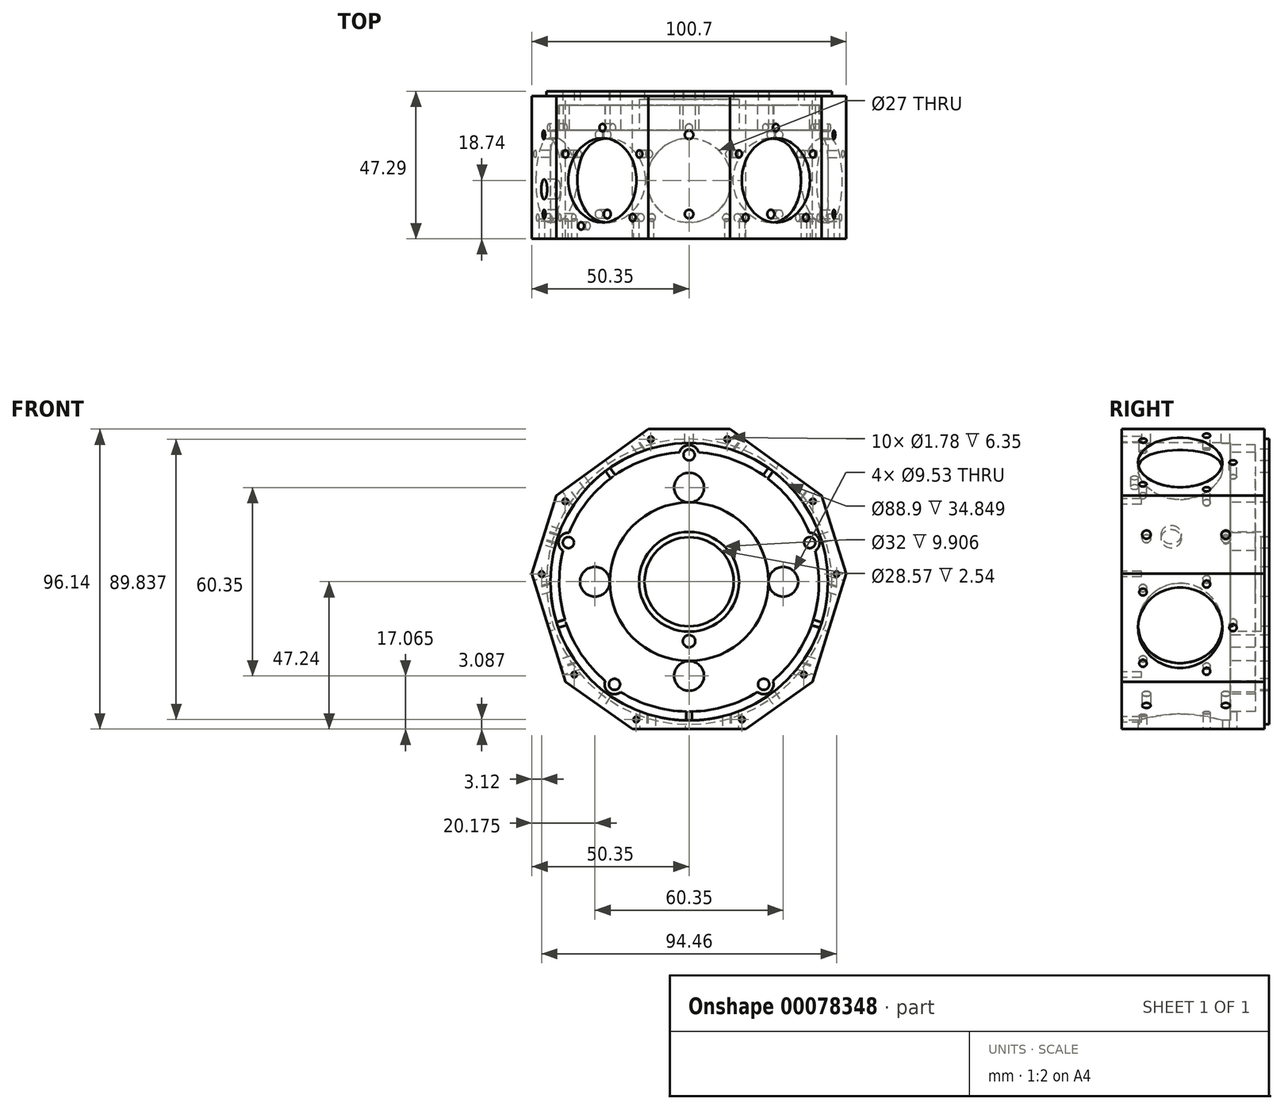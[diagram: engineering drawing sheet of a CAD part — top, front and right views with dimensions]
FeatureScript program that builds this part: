
annotation { "Feature Type Name" : "Feature", "Feature Type Description" : "" }
export const myFeature = defineFeature(function(context is Context, id is Id, definition is map)
    precondition{}
    {
        {
            var Q0;
            Q0=qCreatedBy(makeId("Front.planeOp"),FACE);
            var sketch = newSketch(context, id + "F0", { "sketchPlane" : qUnion([Q0])});
            skLineSegment(sketch, "E0", {"start": v(0, 0) * mm, "end": v(0, 48.9) * mm, "construction": true});
            skCircle(sketch, "E1", {"center": v(0, 0) * mm, "radius": 47.3 * mm, "construction": true});
            skLineSegment(sketch, "E2", {"start": v(0, 0) * mm, "end": v(0, -54.83) * mm, "construction": true});
            skCircle(sketch, "E3", {"center": v(0, 0) * mm, "radius": 44.45 * mm, "construction": true});
            skLineSegment(sketch, "E4", {"start": v(0, 48.9) * mm, "end": v(-13.1, 48.9) * mm});
            skLineSegment(sketch, "E5", {"start": v(-13.1, 48.9) * mm, "end": v(-42.47, 27.58) * mm});
            skLineSegment(sketch, "E6", {"start": v(0, -47.24) * mm, "end": v(-18.14, -47.24) * mm});
            skLineSegment(sketch, "E7", {"start": v(-18.14, -47.24) * mm, "end": v(-39.57, -32.04) * mm});
            skLineSegment(sketch, "E8", {"start": v(-39.57, -32.04) * mm, "end": v(-50.35, 2.64) * mm});
            skLineSegment(sketch, "E9", {"start": v(-50.35, 2.64) * mm, "end": v(-42.47, 27.58) * mm});
            skLineSegment(sketch, "E10.MirrorCS", {"start": v(0, 48.9) * mm, "end": v(13.1, 48.9) * mm});
            skLineSegment(sketch, "E11.MirrorCS", {"start": v(13.1, 48.9) * mm, "end": v(42.47, 27.58) * mm});
            skLineSegment(sketch, "E12.MirrorCS", {"start": v(50.35, 2.64) * mm, "end": v(42.47, 27.58) * mm});
            skLineSegment(sketch, "E13.MirrorCS", {"start": v(39.57, -32.04) * mm, "end": v(50.35, 2.64) * mm});
            skLineSegment(sketch, "E14.MirrorCS", {"start": v(18.14, -47.24) * mm, "end": v(39.57, -32.04) * mm});
            skLineSegment(sketch, "E15.MirrorCS", {"start": v(0, -47.24) * mm, "end": v(18.14, -47.24) * mm});
            skSolve(sketch);
        }
        {
            var Q0;
            Q0 = qSketchRegion(id + "F0", true);
            extrude(context, id + "F1", {"entities" : qUnion([Q0]), "depth" : 47.3 * mm});
        }
        {
            var Q0;
            Q0=makeQuery(id+"F1.opExtrude","CAP_FACE",FACE,{"disambiguationData":[OSD([sQuery(id+"F0.wireOp",EDGE,"E4"),sQuery(id+"F0.wireOp",EDGE,"E5"),sQuery(id+"F0.wireOp",EDGE,"E6"),sQuery(id+"F0.wireOp",EDGE,"E7"),sQuery(id+"F0.wireOp",EDGE,"E8"),sQuery(id+"F0.wireOp",EDGE,"E9"),sQuery(id+"F0.wireOp",EDGE,"E10.MirrorCS"),sQuery(id+"F0.wireOp",EDGE,"E11.MirrorCS"),sQuery(id+"F0.wireOp",EDGE,"E12.MirrorCS"),sQuery(id+"F0.wireOp",EDGE,"E13.MirrorCS"),sQuery(id+"F0.wireOp",EDGE,"E14.MirrorCS"),sQuery(id+"F0.wireOp",EDGE,"E15.MirrorCS")])],"isStart":false});
            var sketch = newSketch(context, id + "F2", { "sketchPlane" : qUnion([Q0])});
            skCircle(sketch, "E16", {"center": v(0, 0) * mm, "radius": 44.45 * mm});
            skSolve(sketch);
        }
        {
            var Q0;
            Q0 = qSketchRegion(id + "F2", true);
            extrude(context, id + "F3", {"entities" : qUnion([Q0]), "operationType" : NewBodyOperationType.REMOVE, "oppositeDirection" : true, "depth" : 34.85 * mm});
        }
        {
            var Q0;
            Q0=makeQuery(id+"F3.boolean.opBoolean","COPY",FACE,{"derivedFrom":makeQuery(id+"F3.opExtrude","CAP_FACE",FACE,{"disambiguationData":[OSD([sQuery(id+"F2.wireOp",EDGE,"E16")])],"isStart":false})});
            var sketch = newSketch(context, id + "F4", { "sketchPlane" : qUnion([Q0])});
            skCircle(sketch, "E17", {"center": v(0, 0) * mm, "radius": 40.64 * mm, "construction": true});
            skArc(sketch, "E18", {"start": v(3.06, 41.48) * mm, "mid": v(0, 43.82) * mm, "end": v(-3.06, 41.48) * mm});
            skArc(sketch, "E19.1.0", {"start": v(-38.5, 15.73) * mm, "mid": v(-41.67, 13.54) * mm, "end": v(-40.4, 9.9) * mm});
            skArc(sketch, "E19.2.0", {"start": v(-26.86, -31.76) * mm, "mid": v(-25.75, -35.45) * mm, "end": v(-21.9, -35.36) * mm});
            skArc(sketch, "E19.3.0", {"start": v(21.9, -35.36) * mm, "mid": v(25.75, -35.45) * mm, "end": v(26.86, -31.76) * mm});
            skArc(sketch, "E19.4.0", {"start": v(40.4, 9.9) * mm, "mid": v(41.67, 13.54) * mm, "end": v(38.5, 15.73) * mm});
            skArc(sketch, "E20", {"start": v(-40.4, 9.9) * mm, "mid": v(-39.56, -12.85) * mm, "end": v(-26.86, -31.76) * mm});
            skArc(sketch, "E21.trimOffspring", {"start": v(-3.06, 41.48) * mm, "mid": v(-24.45, 33.65) * mm, "end": v(-38.5, 15.73) * mm});
            skArc(sketch, "E22.trimOffspring", {"start": v(38.5, 15.73) * mm, "mid": v(24.45, 33.65) * mm, "end": v(3.06, 41.48) * mm});
            skArc(sketch, "E23.trimOffspring", {"start": v(-21.9, -35.36) * mm, "mid": v(0, -41.6) * mm, "end": v(21.9, -35.36) * mm});
            skArc(sketch, "E24.trimOffspring", {"start": v(26.86, -31.76) * mm, "mid": v(39.56, -12.85) * mm, "end": v(40.4, 9.9) * mm});
            skCircle(sketch, "E25", {"center": v(0, 0) * mm, "radius": 25.4 * mm});
            skSolve(sketch);
        }
        {
            var Q0;
            Q0 = qSketchRegion(id + "F4", true);
            extrude(context, id + "F5", {"entities" : qUnion([Q0]), "operationType" : NewBodyOperationType.REMOVE, "oppositeDirection" : true, "depth" : 8 * mm});
        }
        {
            var Q0;
            Q0=makeQuery(id+"F5.boolean.opBoolean","COPY",FACE,{"derivedFrom":makeQuery(id+"F5.opExtrude","CAP_FACE",FACE,{"disambiguationData":[OSD([sQuery(id+"F4.wireOp",EDGE,"E18"),sQuery(id+"F4.wireOp",EDGE,"E19.1.0"),sQuery(id+"F4.wireOp",EDGE,"E19.2.0"),sQuery(id+"F4.wireOp",EDGE,"E19.3.0"),sQuery(id+"F4.wireOp",EDGE,"E19.4.0"),sQuery(id+"F4.wireOp",EDGE,"E20"),sQuery(id+"F4.wireOp",EDGE,"E21.trimOffspring"),sQuery(id+"F4.wireOp",EDGE,"E22.trimOffspring"),sQuery(id+"F4.wireOp",EDGE,"E23.trimOffspring"),sQuery(id+"F4.wireOp",EDGE,"E24.trimOffspring")])],"isStart":false})});
            var sketch = newSketch(context, id + "F6", { "sketchPlane" : qUnion([Q0])});
            skCircle(sketch, "E26", {"center": v(0, 0) * mm, "radius": 40.64 * mm, "construction": true});
            skCircle(sketch, "E27", {"center": v(0, 40.64) * mm, "radius": 1.8 * mm});
            skCircle(sketch, "E28.1.0", {"center": v(-38.65, 12.56) * mm, "radius": 1.8 * mm});
            skCircle(sketch, "E28.2.0", {"center": v(-23.89, -32.88) * mm, "radius": 1.8 * mm});
            skCircle(sketch, "E28.3.0", {"center": v(23.89, -32.88) * mm, "radius": 1.8 * mm});
            skCircle(sketch, "E28.4.0", {"center": v(38.65, 12.56) * mm, "radius": 1.8 * mm});
            skSolve(sketch);
        }
        {
            var Q0;
            Q0 = qSketchRegion(id + "F6", true);
            extrude(context, id + "F7", {"entities" : qUnion([Q0]), "operationType" : NewBodyOperationType.REMOVE, "oppositeDirection" : true, "depth" : 25.4 * mm});
        }
        {
            var Q0;
            Q0=makeQuery(id+"F5.boolean.opBoolean","SPLIT",FACE,{"disambiguationData":[TD([makeQuery(id+"F5.opExtrude","SWEPT_FACE",FACE,{"disambiguationData":[OSD([sQuery(id+"F4.wireOp",EDGE,"E25")])]})])],"derivedFrom":makeQuery(id+"F3.boolean.opBoolean","COPY",FACE,{"derivedFrom":makeQuery(id+"F3.opExtrude","CAP_FACE",FACE,{"disambiguationData":[OSD([sQuery(id+"F2.wireOp",EDGE,"E16")])],"isStart":false})})});
            var sketch = newSketch(context, id + "F8", { "sketchPlane" : qUnion([Q0])});
            skCircle(sketch, "E29", {"center": v(0, 0) * mm, "radius": 16 * mm});
            skSolve(sketch);
        }
        {
            var Q0;
            Q0 = qSketchRegion(id + "F8", true);
            extrude(context, id + "F9", {"entities" : qUnion([Q0]), "operationType" : NewBodyOperationType.REMOVE, "oppositeDirection" : true, "depth" : 9.9 * mm});
        }
        {
            var Q0;
            Q0=makeQuery(id+"F9.boolean.opBoolean","COPY",FACE,{"derivedFrom":makeQuery(id+"F9.opExtrude","CAP_FACE",FACE,{"disambiguationData":[OSD([sQuery(id+"F8.wireOp",EDGE,"E29")])],"isStart":false})});
            var sketch = newSketch(context, id + "F10", { "sketchPlane" : qUnion([Q0])});
            skCircle(sketch, "E30", {"center": v(0, 0) * mm, "radius": 14.29 * mm});
            skSolve(sketch);
        }
        {
            var Q0;
            Q0 = qSketchRegion(id + "F10", true);
            extrude(context, id + "F11", {"entities" : qUnion([Q0]), "operationType" : NewBodyOperationType.REMOVE, "oppositeDirection" : true, "depth" : 25.4 * mm});
        }
        {
            var Q0;
            Q0=makeQuery(id+"F5.boolean.opBoolean","SPLIT",FACE,{"disambiguationData":[TD([makeQuery(id+"F5.opExtrude","SWEPT_FACE",FACE,{"disambiguationData":[OSD([sQuery(id+"F4.wireOp",EDGE,"E25")])]})])],"derivedFrom":makeQuery(id+"F3.boolean.opBoolean","COPY",FACE,{"derivedFrom":makeQuery(id+"F3.opExtrude","CAP_FACE",FACE,{"disambiguationData":[OSD([sQuery(id+"F2.wireOp",EDGE,"E16")])],"isStart":false})})});
            var sketch = newSketch(context, id + "F12", { "sketchPlane" : qUnion([Q0])});
            skLineSegment(sketch, "E31", {"start": v(0, 0) * mm, "end": v(0, -19.05) * mm});
            skCircle(sketch, "E32", {"center": v(0, -19.05) * mm, "radius": 1.98 * mm});
            skSolve(sketch);
        }
        {
            var Q0;
            Q0 = qSketchRegion(id + "F12", true);
            extrude(context, id + "F13", {"entities" : qUnion([Q0]), "operationType" : NewBodyOperationType.REMOVE, "oppositeDirection" : true, "depth" : 25.4 * mm});
        }
        {
            var Q0;
            Q0=makeQuery(id+"F5.boolean.opBoolean","COPY",FACE,{"derivedFrom":makeQuery(id+"F5.opExtrude","CAP_FACE",FACE,{"disambiguationData":[OSD([sQuery(id+"F4.wireOp",EDGE,"E18"),sQuery(id+"F4.wireOp",EDGE,"E19.1.0"),sQuery(id+"F4.wireOp",EDGE,"E19.2.0"),sQuery(id+"F4.wireOp",EDGE,"E19.3.0"),sQuery(id+"F4.wireOp",EDGE,"E19.4.0"),sQuery(id+"F4.wireOp",EDGE,"E20"),sQuery(id+"F4.wireOp",EDGE,"E21.trimOffspring"),sQuery(id+"F4.wireOp",EDGE,"E22.trimOffspring"),sQuery(id+"F4.wireOp",EDGE,"E23.trimOffspring"),sQuery(id+"F4.wireOp",EDGE,"E24.trimOffspring"),sQuery(id+"F4.wireOp",EDGE,"E25")])],"isStart":false})});
            var sketch = newSketch(context, id + "F14", { "sketchPlane" : qUnion([Q0])});
            skCircle(sketch, "E33", {"center": v(0, 0) * mm, "radius": 30.18 * mm, "construction": true});
            skCircle(sketch, "E34", {"center": v(0, 30.18) * mm, "radius": 4.76 * mm});
            skCircle(sketch, "E35.1.0", {"center": v(-30.18, 0) * mm, "radius": 4.76 * mm});
            skCircle(sketch, "E35.2.0", {"center": v(0, -30.18) * mm, "radius": 4.76 * mm});
            skCircle(sketch, "E35.3.0", {"center": v(30.18, 0) * mm, "radius": 4.76 * mm});
            skSolve(sketch);
        }
        {
            var Q0;
            Q0 = qSketchRegion(id + "F14", true);
            var Q1;
            Q1=sQuery(id+"F14.wireOp",EDGE,"E34");
            extrude(context, id + "F15", {"entities" : qUnion([Q0]), "operationType" : NewBodyOperationType.REMOVE, "surfaceEntities" : qUnion([Q1]), "oppositeDirection" : true, "depth" : 25.4 * mm});
        }
        {
            var Q0;
            Q0=makeQuery(id+"F1.opExtrude","SWEPT_FACE",FACE,{"disambiguationData":[OSD([sQuery(id+"F0.wireOp",EDGE,"E6"),sQuery(id+"F0.wireOp",EDGE,"E15.MirrorCS")])]});
            var sketch = newSketch(context, id + "F16", { "sketchPlane" : qUnion([Q0])});
            skLineSegment(sketch, "E36", {"start": v(0, 0) * mm, "end": v(0, 28.55) * mm, "construction": true});
            skCircle(sketch, "E37", {"center": v(0, 28.55) * mm, "radius": 13.5 * mm});
            skCircle(sketch, "E38", {"center": v(0, 28.55) * mm, "radius": 16.9 * mm, "construction": true});
            skCircle(sketch, "E39", {"center": v(-14.63, 20.1) * mm, "radius": 1.2 * mm});
            skCircle(sketch, "E40", {"center": v(-11.94, 40.5) * mm, "radius": 1.2 * mm});
            skCircle(sketch, "E41.MirrorC", {"center": v(14.63, 20.1) * mm, "radius": 1.2 * mm});
            skCircle(sketch, "E42.MirrorC", {"center": v(11.94, 40.5) * mm, "radius": 1.2 * mm});
            skCircle(sketch, "E43", {"center": v(0, 11.66) * mm, "radius": 1.2 * mm});
            skSolve(sketch);
        }
        {
            var Q0;
            Q0 = qSketchRegion(id + "F16", true);
            extrude(context, id + "F17", {"entities" : qUnion([Q0]), "operationType" : NewBodyOperationType.REMOVE, "oppositeDirection" : true, "depth" : 13.37 * mm});
        }
        {
            var Q0;
            Q0=makeQuery(id+"F1.opExtrude","SWEPT_FACE",FACE,{"disambiguationData":[OSD([sQuery(id+"F0.wireOp",EDGE,"E8")])]});
            var sketch = newSketch(context, id + "F18", { "sketchPlane" : qUnion([Q0])});
            skLineSegment(sketch, "E44", {"start": v(0, -18.85) * mm, "end": v(0, 17.47) * mm});
            skLineSegment(sketch, "E45", {"start": v(0, -0.69) * mm, "end": v(28.55, -0.69) * mm, "construction": true});
            skCircle(sketch, "E46", {"center": v(28.55, -0.69) * mm, "radius": 13.5 * mm});
            skCircle(sketch, "E47", {"center": v(28.55, -0.69) * mm, "radius": 16.9 * mm, "construction": true});
            skCircle(sketch, "E48", {"center": v(40.5, 11.25) * mm, "radius": 1.2 * mm});
            skCircle(sketch, "E49", {"center": v(20.1, 13.94) * mm, "radius": 1.2 * mm});
            skCircle(sketch, "E50.MirrorC", {"center": v(40.5, -12.63) * mm, "radius": 1.2 * mm});
            skCircle(sketch, "E51.MirrorC", {"center": v(20.1, -15.32) * mm, "radius": 1.2 * mm});
            skCircle(sketch, "E52", {"center": v(11.66, -0.69) * mm, "radius": 1.2 * mm});
            skSolve(sketch);
        }
        {
            var Q0;
            Q0 = qSketchRegion(id + "F18", true);
            extrude(context, id + "F19", {"entities" : qUnion([Q0]), "operationType" : NewBodyOperationType.REMOVE, "oppositeDirection" : true, "depth" : 7.62 * mm});
        }
        {
            var Q0;
            Q0=makeQuery(id+"F1.opExtrude","SWEPT_FACE",FACE,{"disambiguationData":[OSD([sQuery(id+"F0.wireOp",EDGE,"E5")])]});
            var sketch = newSketch(context, id + "F20", { "sketchPlane" : qUnion([Q0])});
            skLineSegment(sketch, "E53", {"start": v(18.11, 0) * mm, "end": v(-0.03, 0) * mm, "construction": true});
            skLineSegment(sketch, "E54", {"start": v(0, 0) * mm, "end": v(0, -28.55) * mm, "construction": true});
            skCircle(sketch, "E55", {"center": v(0, -28.55) * mm, "radius": 13.5 * mm});
            skCircle(sketch, "E56", {"center": v(0, -28.55) * mm, "radius": 16.9 * mm, "construction": true});
            skLineSegment(sketch, "E57", {"start": v(0, -28.55) * mm, "end": v(18.05, -18.13) * mm, "construction": true});
            skLineSegment(sketch, "E58", {"start": v(0, -28.55) * mm, "end": v(16.7, -45.24) * mm, "construction": true});
            skCircle(sketch, "E59", {"center": v(14.63, -20.1) * mm, "radius": 1.2 * mm});
            skCircle(sketch, "E60", {"center": v(11.94, -40.5) * mm, "radius": 1.2 * mm});
            skLineSegment(sketch, "E61.MirrorCS", {"start": v(-28.55, -28.55) * mm, "end": v(0, -28.55) * mm, "construction": true});
            skCircle(sketch, "E62.MirrorC", {"center": v(-8.45, -43.18) * mm, "radius": 1.2 * mm});
            skCircle(sketch, "E63.MirrorC", {"center": v(-14.63, -20.1) * mm, "radius": 1.2 * mm});
            skCircle(sketch, "E64", {"center": v(0, -11.66) * mm, "radius": 1.2 * mm});
            skSolve(sketch);
        }
        {
            var Q0;
            Q0 = qSketchRegion(id + "F20", true);
            extrude(context, id + "F21", {"entities" : qUnion([Q0]), "operationType" : NewBodyOperationType.REMOVE, "oppositeDirection" : true, "depth" : 7.62 * mm});
        }
        {
            var Q0;
            Q0=makeQuery(id+"F1.opExtrude","SWEPT_FACE",FACE,{"disambiguationData":[OSD([sQuery(id+"F0.wireOp",EDGE,"E13.MirrorCS")])]});
            var sketch = newSketch(context, id + "F22", { "sketchPlane" : qUnion([Q0])});
            skLineSegment(sketch, "E65", {"start": v(0, -18.85) * mm, "end": v(0, -0.7) * mm, "construction": true});
            skLineSegment(sketch, "E66", {"start": v(0, -0.7) * mm, "end": v(-28.55, -0.7) * mm, "construction": true});
            skCircle(sketch, "E67", {"center": v(-28.55, -0.7) * mm, "radius": 13.5 * mm});
            skCircle(sketch, "E68", {"center": v(-28.55, -0.7) * mm, "radius": 16.9 * mm, "construction": true});
            skLineSegment(sketch, "E69", {"start": v(-28.55, -0.7) * mm, "end": v(-18.13, -18.75) * mm, "construction": true});
            skLineSegment(sketch, "E70", {"start": v(-28.55, -0.7) * mm, "end": v(-42.9, -15.06) * mm, "construction": true});
            skCircle(sketch, "E71", {"center": v(-40.5, -12.65) * mm, "radius": 1.2 * mm});
            skCircle(sketch, "E72", {"center": v(-20.1, -15.33) * mm, "radius": 1.2 * mm});
            skCircle(sketch, "E73.MirrorC", {"center": v(-40.5, 11.24) * mm, "radius": 1.2 * mm});
            skCircle(sketch, "E74.MirrorC", {"center": v(-20.1, 13.92) * mm, "radius": 1.2 * mm});
            skCircle(sketch, "E75", {"center": v(-11.66, -0.7) * mm, "radius": 1.2 * mm});
            skSolve(sketch);
        }
        {
            var Q0;
            Q0 = qSketchRegion(id + "F22", true);
            extrude(context, id + "F23", {"entities" : qUnion([Q0]), "operationType" : NewBodyOperationType.REMOVE, "oppositeDirection" : true, "depth" : 7.62 * mm});
        }
        {
            var Q0;
            Q0=makeQuery(id+"F1.opExtrude","SWEPT_FACE",FACE,{"disambiguationData":[OSD([sQuery(id+"F0.wireOp",EDGE,"E11.MirrorCS")])]});
            var sketch = newSketch(context, id + "F24", { "sketchPlane" : qUnion([Q0])});
            skLineSegment(sketch, "E76", {"start": v(18.18, 0) * mm, "end": v(0.03, 0) * mm, "construction": true});
            skLineSegment(sketch, "E77", {"start": v(0.03, 0) * mm, "end": v(0.03, -28.55) * mm, "construction": true});
            skCircle(sketch, "E78", {"center": v(0.03, -28.55) * mm, "radius": 13.5 * mm});
            skCircle(sketch, "E79", {"center": v(0.03, -28.55) * mm, "radius": 16.9 * mm, "construction": true});
            skLineSegment(sketch, "E80", {"start": v(0.03, -28.55) * mm, "end": v(20.12, -16.95) * mm, "construction": true});
            skLineSegment(sketch, "E81", {"start": v(0.03, -28.55) * mm, "end": v(17.3, -45.82) * mm, "construction": true});
            skCircle(sketch, "E82", {"center": v(11.98, -40.5) * mm, "radius": 1.2 * mm});
            skCircle(sketch, "E83", {"center": v(14.66, -20.1) * mm, "radius": 1.2 * mm});
            skCircle(sketch, "E84.MirrorC", {"center": v(-11.91, -40.5) * mm, "radius": 1.2 * mm});
            skCircle(sketch, "E85.MirrorC", {"center": v(-14.6, -20.1) * mm, "radius": 1.2 * mm});
            skCircle(sketch, "E86", {"center": v(0.03, -11.66) * mm, "radius": 1.2 * mm});
            skSolve(sketch);
        }
        {
            var Q0;
            Q0 = qSketchRegion(id + "F24", true);
            extrude(context, id + "F25", {"entities" : qUnion([Q0]), "operationType" : NewBodyOperationType.REMOVE, "oppositeDirection" : true, "depth" : 7.62 * mm});
        }
        {
            var Q0;
            Q0=makeQuery(id+"F1.opExtrude","SWEPT_FACE",FACE,{"disambiguationData":[OSD([sQuery(id+"F0.wireOp",EDGE,"E9")])]});
            var sketch = newSketch(context, id + "F26", { "sketchPlane" : qUnion([Q0])});
            skCircle(sketch, "E87", {"center": v(13.97, 0) * mm, "radius": 1.39 * mm});
            skCircle(sketch, "E88", {"center": v(31.45, 0.43) * mm, "radius": 3.18 * mm});
            skCircle(sketch, "E89", {"center": v(39.37, 0.43) * mm, "radius": 1.39 * mm});
            skSolve(sketch);
        }
        {
            var Q0;
            Q0 = qSketchRegion(id + "F26", true);
            extrude(context, id + "F27", {"entities" : qUnion([Q0]), "operationType" : NewBodyOperationType.REMOVE, "oppositeDirection" : true, "depth" : 7.62 * mm});
        }
        {
            var Q0;
            Q0=makeQuery(id+"F1.opExtrude","SWEPT_FACE",FACE,{"disambiguationData":[OSD([sQuery(id+"F0.wireOp",EDGE,"E4"),sQuery(id+"F0.wireOp",EDGE,"E10.MirrorCS")])]});
            var sketch = newSketch(context, id + "F28", { "sketchPlane" : qUnion([Q0])});
            skCircle(sketch, "E90", {"center": v(0, -13.97) * mm, "radius": 1.39 * mm});
            skCircle(sketch, "E91", {"center": v(0, -39.37) * mm, "radius": 1.39 * mm});
            skSolve(sketch);
        }
        {
            var Q0;
            Q0 = qSketchRegion(id + "F28", true);
            extrude(context, id + "F29", {"entities" : qUnion([Q0]), "operationType" : NewBodyOperationType.REMOVE, "oppositeDirection" : true, "depth" : 7.62 * mm});
        }
        {
            var Q0;
            Q0=makeQuery(id+"F1.opExtrude","SWEPT_FACE",FACE,{"disambiguationData":[OSD([sQuery(id+"F0.wireOp",EDGE,"E12.MirrorCS")])]});
            var sketch = newSketch(context, id + "F30", { "sketchPlane" : qUnion([Q0])});
            skCircle(sketch, "E92", {"center": v(-13.97, 0.44) * mm, "radius": 1.39 * mm});
            skCircle(sketch, "E93", {"center": v(-39.37, 0.44) * mm, "radius": 1.39 * mm});
            skSolve(sketch);
        }
        {
            var Q0;
            Q0 = qSketchRegion(id + "F30", true);
            extrude(context, id + "F31", {"entities" : qUnion([Q0]), "operationType" : NewBodyOperationType.REMOVE, "oppositeDirection" : true, "depth" : 7.62 * mm});
        }
        {
            var Q0;
            Q0=makeQuery(id+"F1.opExtrude","SWEPT_FACE",FACE,{"disambiguationData":[OSD([sQuery(id+"F0.wireOp",EDGE,"E14.MirrorCS")])]});
            var sketch = newSketch(context, id + "F32", { "sketchPlane" : qUnion([Q0])});
            skLineSegment(sketch, "E94", {"start": v(0.59, 47.3) * mm, "end": v(0.59, 47.21) * mm});
            skCircle(sketch, "E95", {"center": v(0.59, 13.97) * mm, "radius": 1.39 * mm});
            skCircle(sketch, "E96", {"center": v(0.59, 39.37) * mm, "radius": 1.39 * mm});
            skSolve(sketch);
        }
        {
            var Q0;
            Q0 = qSketchRegion(id + "F32", true);
            extrude(context, id + "F33", {"entities" : qUnion([Q0]), "operationType" : NewBodyOperationType.REMOVE, "oppositeDirection" : true, "depth" : 7.62 * mm});
        }
        {
            var Q0;
            Q0=makeQuery(id+"F1.opExtrude","SWEPT_FACE",FACE,{"disambiguationData":[OSD([sQuery(id+"F0.wireOp",EDGE,"E7")])]});
            var sketch = newSketch(context, id + "F34", { "sketchPlane" : qUnion([Q0])});
            skCircle(sketch, "E97", {"center": v(-0.6, 13.97) * mm, "radius": 1.39 * mm});
            skCircle(sketch, "E98", {"center": v(-0.6, 39.37) * mm, "radius": 1.39 * mm});
            skSolve(sketch);
        }
        {
            var Q0;
            Q0 = qSketchRegion(id + "F34", true);
            extrude(context, id + "F35", {"entities" : qUnion([Q0]), "operationType" : NewBodyOperationType.REMOVE, "oppositeDirection" : true, "depth" : 7.62 * mm});
        }
        {
            var Q0;
            Q0=makeQuery(id+"F1.opExtrude","CAP_FACE",FACE,{"disambiguationData":[OSD([sQuery(id+"F0.wireOp",EDGE,"E4"),sQuery(id+"F0.wireOp",EDGE,"E5"),sQuery(id+"F0.wireOp",EDGE,"E6"),sQuery(id+"F0.wireOp",EDGE,"E7"),sQuery(id+"F0.wireOp",EDGE,"E8"),sQuery(id+"F0.wireOp",EDGE,"E9"),sQuery(id+"F0.wireOp",EDGE,"E10.MirrorCS"),sQuery(id+"F0.wireOp",EDGE,"E11.MirrorCS"),sQuery(id+"F0.wireOp",EDGE,"E12.MirrorCS"),sQuery(id+"F0.wireOp",EDGE,"E13.MirrorCS"),sQuery(id+"F0.wireOp",EDGE,"E14.MirrorCS"),sQuery(id+"F0.wireOp",EDGE,"E15.MirrorCS")])],"isStart":false});
            var sketch = newSketch(context, id + "F36", { "sketchPlane" : qUnion([Q0])});
            skCircle(sketch, "E99", {"center": v(-12.24, 45.68) * mm, "radius": 0.89 * mm});
            skCircle(sketch, "E100", {"center": v(-39.66, 25.76) * mm, "radius": 0.89 * mm});
            skCircle(sketch, "E101", {"center": v(-47.23, 2.48) * mm, "radius": 0.89 * mm});
            skCircle(sketch, "E102", {"center": v(-36.75, -29.76) * mm, "radius": 0.89 * mm});
            skCircle(sketch, "E103", {"center": v(-16.95, -44.15) * mm, "radius": 0.89 * mm});
            skCircle(sketch, "E104.MirrorC", {"center": v(47.23, 2.48) * mm, "radius": 0.89 * mm});
            skCircle(sketch, "E105.MirrorC", {"center": v(36.75, -29.76) * mm, "radius": 0.89 * mm});
            skCircle(sketch, "E106.MirrorC", {"center": v(16.95, -44.15) * mm, "radius": 0.89 * mm});
            skCircle(sketch, "E107.MirrorC", {"center": v(39.66, 25.76) * mm, "radius": 0.89 * mm});
            skCircle(sketch, "E108.MirrorC", {"center": v(12.24, 45.68) * mm, "radius": 0.89 * mm});
            skSolve(sketch);
        }
        {
            var Q0;
            Q0=makeQuery(id+"F1.opExtrude","CAP_FACE",FACE,{"disambiguationData":[OSD([sQuery(id+"F0.wireOp",EDGE,"E4"),sQuery(id+"F0.wireOp",EDGE,"E5"),sQuery(id+"F0.wireOp",EDGE,"E6"),sQuery(id+"F0.wireOp",EDGE,"E7"),sQuery(id+"F0.wireOp",EDGE,"E8"),sQuery(id+"F0.wireOp",EDGE,"E9"),sQuery(id+"F0.wireOp",EDGE,"E10.MirrorCS"),sQuery(id+"F0.wireOp",EDGE,"E11.MirrorCS"),sQuery(id+"F0.wireOp",EDGE,"E12.MirrorCS"),sQuery(id+"F0.wireOp",EDGE,"E13.MirrorCS"),sQuery(id+"F0.wireOp",EDGE,"E14.MirrorCS"),sQuery(id+"F0.wireOp",EDGE,"E15.MirrorCS")])],"isStart":true});
            var sketch = newSketch(context, id + "F37", { "sketchPlane" : qUnion([Q0])});
            skCircle(sketch, "E109", {"center": v(0, 0) * mm, "radius": 45.72 * mm});
            skCircle(sketch, "E110", {"center": v(0, 0) * mm, "radius": 57.87 * mm});
            skSolve(sketch);
        }
        {
            var Q0;
            Q0=makeQuery(id+"F37.imprint","IMPRINT",FACE,{"disambiguationData":[TD([[makeQuery(id+"F37.imprint","IMPRINT",EDGE,{"derivedFrom":sQuery(id+"F37.wireOp",EDGE,"E110")}),1.0]])]});
            var Q1;
            Q1=makeQuery(id+"F37.imprint","IMPRINT",FACE,{"disambiguationData":[TD([[makeQuery(id+"F37.imprint","IMPRINT",EDGE,{"derivedFrom":sQuery(id+"F37.wireOp",EDGE,"E109")}),-1.0]])]});
            extrude(context, id + "F38", {"entities" : qUnion([Q0, Q1]), "operationType" : NewBodyOperationType.REMOVE, "oppositeDirection" : true, "depth" : 1.57 * mm});
        }
        {
            var Q0;
            Q0 = qSketchRegion(id + "F36", true);
            extrude(context, id + "F39", {"entities" : qUnion([Q0]), "operationType" : NewBodyOperationType.REMOVE, "oppositeDirection" : true, "depth" : 6.35 * mm});
        }
        {
            var Q0;
            Q0=qCreatedBy(makeId("Top.planeOp"),FACE);
            var sketch = newSketch(context, id + "F40", { "sketchPlane" : qUnion([Q0])});
            skLineSegment(sketch, "E111", {"start": v(0, 45.6) * mm, "end": v(0, -69.38) * mm, "construction": true});
            skSolve(sketch);
        }
    });
